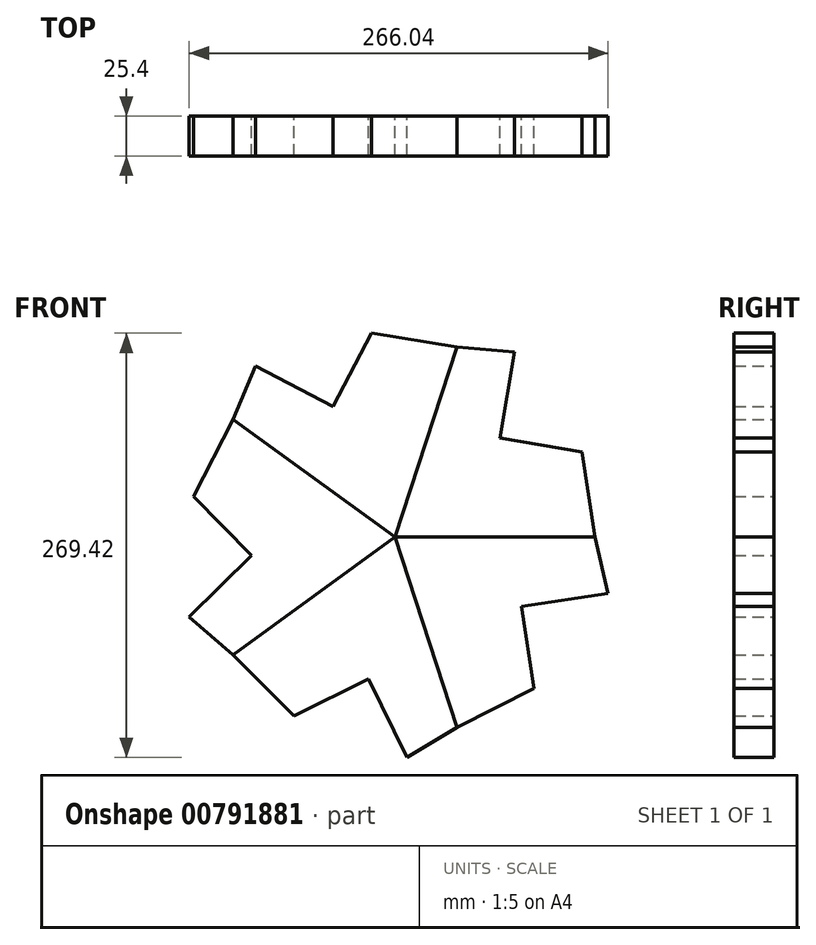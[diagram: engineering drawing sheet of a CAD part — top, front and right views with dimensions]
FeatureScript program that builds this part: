
annotation { "Feature Type Name" : "Feature", "Feature Type Description" : "" }
export const myFeature = defineFeature(function(context is Context, id is Id, definition is map)
    precondition{}
    {
        {
            var Q0;
            Q0=qCreatedBy(makeId("Front.planeOp"),FACE);
            var sketch = newSketch(context, id + "F0", { "sketchPlane" : qUnion([Q0])});
            skLineSegment(sketch, "E0", {"start": v(0, 0) * mm, "end": v(127, 0) * mm});
            skLineSegment(sketch, "E1", {"start": v(0, 0) * mm, "end": v(39.25, 120.78) * mm});
            skLineSegment(sketch, "E2", {"start": v(39.25, 120.78) * mm, "end": v(75.93, 117.71) * mm});
            skLineSegment(sketch, "E3", {"start": v(75.93, 117.71) * mm, "end": v(66.68, 62.95) * mm});
            skLineSegment(sketch, "E4", {"start": v(66.68, 62.95) * mm, "end": v(118.62, 54.18) * mm});
            skLineSegment(sketch, "E5", {"start": v(118.62, 54.18) * mm, "end": v(127, 0) * mm});
            skSolve(sketch);
        }
        {
            var Q0;
            Q0=makeQuery(id+"F0.imprint","IMPRINT",FACE,{"disambiguationData":[TD([[makeQuery(id+"F0.imprint","IMPRINT",EDGE,{"derivedFrom":sQuery(id+"F0.wireOp",EDGE,"E0")}),1.0]])]});
            extrude(context, id + "F1", {"entities" : qUnion([Q0]), "depth" : 25.4 * mm, "offsetDistance" : 25.4 * mm});
        }
        {
            var Q0;
            Q0=makeQuery(id+"F1.opExtrude","SWEPT_BODY",BODY,{"disambiguationData":[OSD([sQuery(id+"F0.wireOp",EDGE,"E0"),sQuery(id+"F0.wireOp",EDGE,"E1"),sQuery(id+"F0.wireOp",EDGE,"E2"),sQuery(id+"F0.wireOp",EDGE,"E3"),sQuery(id+"F0.wireOp",EDGE,"E4"),sQuery(id+"F0.wireOp",EDGE,"E5")])]});
            var Q1;
            Q1=makeQuery(id+"F1.opExtrude","SWEPT_EDGE",EDGE,{"disambiguationData":[OSD([sQuery(id+"F0.wireOp",EDGE,"E0"),sQuery(id+"F0.wireOp",EDGE,"E1")])]});
            circularPattern(context, id + "F2", {"entities" : qUnion([Q0]), "axis" : qUnion([Q1]), "angle" : 360 * degree, "instanceCount" : 5, "equalSpace" : true});
        }
    });
